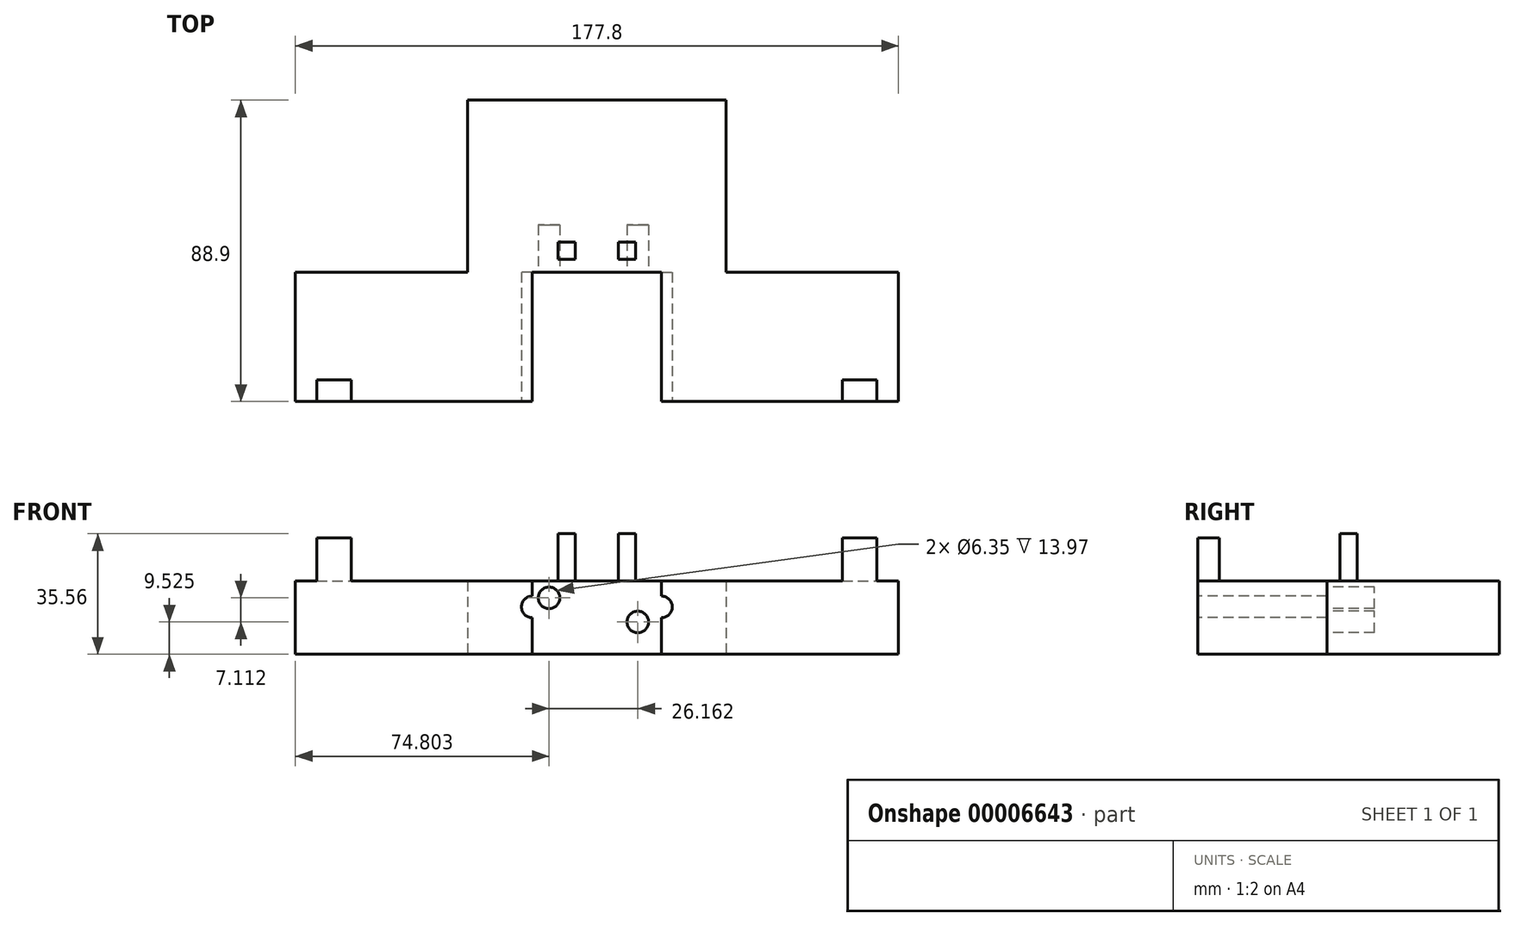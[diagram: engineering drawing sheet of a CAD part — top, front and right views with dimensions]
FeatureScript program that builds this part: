
annotation { "Feature Type Name" : "Feature", "Feature Type Description" : "" }
export const myFeature = defineFeature(function(context is Context, id is Id, definition is map)
    precondition{}
    {
        {
            var Q0;
            Q0=qCreatedBy(makeId("Front.planeOp"),FACE);
            var sketch = newSketch(context, id + "F0", { "sketchPlane" : qUnion([Q0])});
            skLineSegment(sketch, "E0.bottom", {"start": v(-19.05, 2.54) * mm, "end": v(19.05, 2.54) * mm});
            skLineSegment(sketch, "E0.top", {"start": v(-19.05, -19.05) * mm, "end": v(19.05, -19.05) * mm});
            skLineSegment(sketch, "E0.left", {"start": v(-19.05, 2.54) * mm, "end": v(-19.05, -19.05) * mm});
            skLineSegment(sketch, "E0.right", {"start": v(19.05, 2.54) * mm, "end": v(19.05, -19.05) * mm});
            skLineSegment(sketch, "E1.bottom", {"start": v(-38.1, 2.54) * mm, "end": v(38.1, 2.54) * mm});
            skLineSegment(sketch, "E1.top", {"start": v(-38.1, -19.05) * mm, "end": v(38.1, -19.05) * mm});
            skLineSegment(sketch, "E1.left", {"start": v(-38.1, 2.54) * mm, "end": v(-38.1, -19.05) * mm});
            skLineSegment(sketch, "E1.right", {"start": v(38.1, 2.54) * mm, "end": v(38.1, -19.05) * mm});
            skSolve(sketch);
        }
        {
            var Q0;
            {var subQ2=sQuery(id+"F0.wireOp",EDGE,"E0.left");Q0=makeQuery(id+"F0.imprint","IMPRINT",FACE,{"disambiguationData":[TD([[makeQuery(id+"F0.imprint","IMPRINT",EDGE,{"derivedFrom":subQ2}),-1.0]])]});}
            var Q1;
            {var subQ2=sQuery(id+"F0.wireOp",EDGE,"E0.left");Q1=makeQuery(id+"F0.imprint","IMPRINT",FACE,{"disambiguationData":[TD([[makeQuery(id+"F0.imprint","IMPRINT",EDGE,{"derivedFrom":subQ2}),1.0]])]});}
            var Q2;
            {var subQ2=sQuery(id+"F0.wireOp",EDGE,"E0.right");Q2=makeQuery(id+"F0.imprint","IMPRINT",FACE,{"disambiguationData":[TD([[makeQuery(id+"F0.imprint","IMPRINT",EDGE,{"derivedFrom":subQ2}),1.0]])]});}
            extrude(context, id + "F1", {"entities" : qUnion([Q0, Q1, Q2]), "depth" : 50.8 * mm});
        }
        {
            var Q0;
            Q0=makeQuery(id+"F1.opExtrude","CAP_FACE",FACE,{"disambiguationData":[OSD([sQuery(id+"F0.wireOp",EDGE,"E1.bottom"),sQuery(id+"F0.wireOp",EDGE,"E1.top"),sQuery(id+"F0.wireOp",EDGE,"E1.left"),sQuery(id+"F0.wireOp",EDGE,"E1.right")])],"isStart":false});
            var sketch = newSketch(context, id + "F2", { "sketchPlane" : qUnion([Q0])});
            skLineSegment(sketch, "E2.bottom", {"start": v(-19.05, 2.54) * mm, "end": v(-88.9, 2.54) * mm});
            skLineSegment(sketch, "E2.top", {"start": v(-19.05, -19.05) * mm, "end": v(-88.9, -19.05) * mm});
            skLineSegment(sketch, "E2.left", {"start": v(-19.05, 2.54) * mm, "end": v(-19.05, -19.05) * mm});
            skLineSegment(sketch, "E2.right", {"start": v(-88.9, 2.54) * mm, "end": v(-88.9, -19.05) * mm});
            skLineSegment(sketch, "E3.bottom", {"start": v(19.05, 2.54) * mm, "end": v(88.9, 2.54) * mm});
            skLineSegment(sketch, "E3.top", {"start": v(19.05, -19.05) * mm, "end": v(88.9, -19.05) * mm});
            skLineSegment(sketch, "E3.left", {"start": v(19.05, 2.54) * mm, "end": v(19.05, -19.05) * mm});
            skLineSegment(sketch, "E3.right", {"start": v(88.9, 2.54) * mm, "end": v(88.9, -19.05) * mm});
            skSolve(sketch);
        }
        {
            var Q0;
            Q0 = qSketchRegion(id + "F2", true);
            extrude(context, id + "F3", {"entities" : qUnion([Q0]), "operationType" : NewBodyOperationType.ADD, "depth" : 38.1 * mm});
        }
        {
            var Q0;
            Q0=makeQuery(id+"F3.opExtrude","CAP_FACE",FACE,{"disambiguationData":[OSD([sQuery(id+"F2.wireOp",EDGE,"E2.bottom"),sQuery(id+"F2.wireOp",EDGE,"E2.top"),sQuery(id+"F2.wireOp",EDGE,"E2.left"),sQuery(id+"F2.wireOp",EDGE,"E2.right")])],"isStart":false});
            var sketch = newSketch(context, id + "F4", { "sketchPlane" : qUnion([Q0])});
            skCircle(sketch, "E4", {"center": v(-19.05, -5.08) * mm, "radius": 3.18 * mm});
            skCircle(sketch, "E5", {"center": v(19.05, -5.08) * mm, "radius": 3.18 * mm});
            skSolve(sketch);
        }
        {
            var Q0;
            Q0 = qSketchRegion(id + "F4", true);
            extrude(context, id + "F5", {"entities" : qUnion([Q0]), "operationType" : NewBodyOperationType.REMOVE, "oppositeDirection" : true, "depth" : 38.1 * mm});
        }
        {
            var Q0;
            Q0=makeQuery(id+"F5.boolean.opBoolean","MERGE",FACE,{"derivedFrom":[makeQuery(id+"F1.opExtrude","CAP_FACE",FACE,{"disambiguationData":[OSD([sQuery(id+"F0.wireOp",EDGE,"E1.bottom"),sQuery(id+"F0.wireOp",EDGE,"E1.top"),sQuery(id+"F0.wireOp",EDGE,"E1.left"),sQuery(id+"F0.wireOp",EDGE,"E1.right")])],"isStart":false}),makeQuery(id+"F5.opExtrude","CAP_FACE",FACE,{"disambiguationData":[OSD([sQuery(id+"F4.wireOp",EDGE,"E4")])],"isStart":false}),makeQuery(id+"F5.opExtrude","CAP_FACE",FACE,{"disambiguationData":[OSD([sQuery(id+"F4.wireOp",EDGE,"E5")])],"isStart":false})]});
            var sketch = newSketch(context, id + "F6", { "sketchPlane" : qUnion([Q0])});
            skCircle(sketch, "E6", {"center": v(-14.1, -2.41) * mm, "radius": 3.17 * mm});
            skCircle(sketch, "E7", {"center": v(12.07, -9.53) * mm, "radius": 3.18 * mm});
            skSolve(sketch);
        }
        {
            var Q0;
            Q0 = qSketchRegion(id + "F6", true);
            extrude(context, id + "F7", {"entities" : qUnion([Q0]), "operationType" : NewBodyOperationType.REMOVE, "oppositeDirection" : true, "depth" : 13.97 * mm});
        }
        {
            var Q0;
            Q0=makeQuery(id+"F3.boolean.opBoolean","MERGE",FACE,{"derivedFrom":[makeQuery(id+"F1.opExtrude","SWEPT_FACE",FACE,{"disambiguationData":[OSD([sQuery(id+"F0.wireOp",EDGE,"E1.bottom")])]}),makeQuery(id+"F3.opExtrude","SWEPT_FACE",FACE,{"disambiguationData":[OSD([sQuery(id+"F2.wireOp",EDGE,"E2.bottom")])]}),makeQuery(id+"F3.opExtrude","SWEPT_FACE",FACE,{"disambiguationData":[OSD([sQuery(id+"F2.wireOp",EDGE,"E3.bottom")])]})]});
            var sketch = newSketch(context, id + "F8", { "sketchPlane" : qUnion([Q0])});
            skLineSegment(sketch, "E8.bottom", {"start": v(-11.43, -41.91) * mm, "end": v(-6.35, -41.91) * mm});
            skLineSegment(sketch, "E8.top", {"start": v(-11.43, -47) * mm, "end": v(-6.35, -47) * mm});
            skLineSegment(sketch, "E8.left", {"start": v(-11.43, -41.91) * mm, "end": v(-11.43, -47) * mm});
            skLineSegment(sketch, "E8.right", {"start": v(-6.35, -41.91) * mm, "end": v(-6.35, -47) * mm});
            skLineSegment(sketch, "E9.bottom", {"start": v(6.35, -41.91) * mm, "end": v(11.43, -41.91) * mm});
            skLineSegment(sketch, "E9.top", {"start": v(6.35, -47) * mm, "end": v(11.43, -47) * mm});
            skLineSegment(sketch, "E9.left", {"start": v(6.35, -41.91) * mm, "end": v(6.35, -47) * mm});
            skLineSegment(sketch, "E9.right", {"start": v(11.43, -41.91) * mm, "end": v(11.43, -47) * mm});
            skSolve(sketch);
        }
        {
            var Q0;
            Q0 = qSketchRegion(id + "F8", true);
            extrude(context, id + "F9", {"entities" : qUnion([Q0]), "operationType" : NewBodyOperationType.ADD, "depth" : 13.97 * mm});
        }
        {
            var Q0;
            Q0=makeQuery(id+"F3.boolean.opBoolean","MERGE",FACE,{"derivedFrom":[makeQuery(id+"F1.opExtrude","SWEPT_FACE",FACE,{"disambiguationData":[OSD([sQuery(id+"F0.wireOp",EDGE,"E1.bottom")])]}),makeQuery(id+"F3.opExtrude","SWEPT_FACE",FACE,{"disambiguationData":[OSD([sQuery(id+"F2.wireOp",EDGE,"E2.bottom")])]}),makeQuery(id+"F3.opExtrude","SWEPT_FACE",FACE,{"disambiguationData":[OSD([sQuery(id+"F2.wireOp",EDGE,"E3.bottom")])]})]});
            var sketch = newSketch(context, id + "F10", { "sketchPlane" : qUnion([Q0])});
            skLineSegment(sketch, "E10.bottom", {"start": v(-82.55, -82.55) * mm, "end": v(-72.4, -82.55) * mm});
            skLineSegment(sketch, "E10.top", {"start": v(-82.55, -88.9) * mm, "end": v(-72.4, -88.9) * mm});
            skLineSegment(sketch, "E10.left", {"start": v(-82.55, -82.55) * mm, "end": v(-82.55, -88.9) * mm});
            skLineSegment(sketch, "E10.right", {"start": v(-72.4, -82.55) * mm, "end": v(-72.4, -88.9) * mm});
            skLineSegment(sketch, "E11.bottom", {"start": v(72.4, -82.55) * mm, "end": v(82.55, -82.55) * mm});
            skLineSegment(sketch, "E11.top", {"start": v(72.4, -88.9) * mm, "end": v(82.55, -88.9) * mm});
            skLineSegment(sketch, "E11.left", {"start": v(72.4, -82.55) * mm, "end": v(72.4, -88.9) * mm});
            skLineSegment(sketch, "E11.right", {"start": v(82.55, -82.55) * mm, "end": v(82.55, -88.9) * mm});
            skSolve(sketch);
        }
        {
            var Q0;
            Q0 = qSketchRegion(id + "F10", true);
            extrude(context, id + "F11", {"entities" : qUnion([Q0]), "operationType" : NewBodyOperationType.ADD, "depth" : 12.7 * mm});
        }
    });
